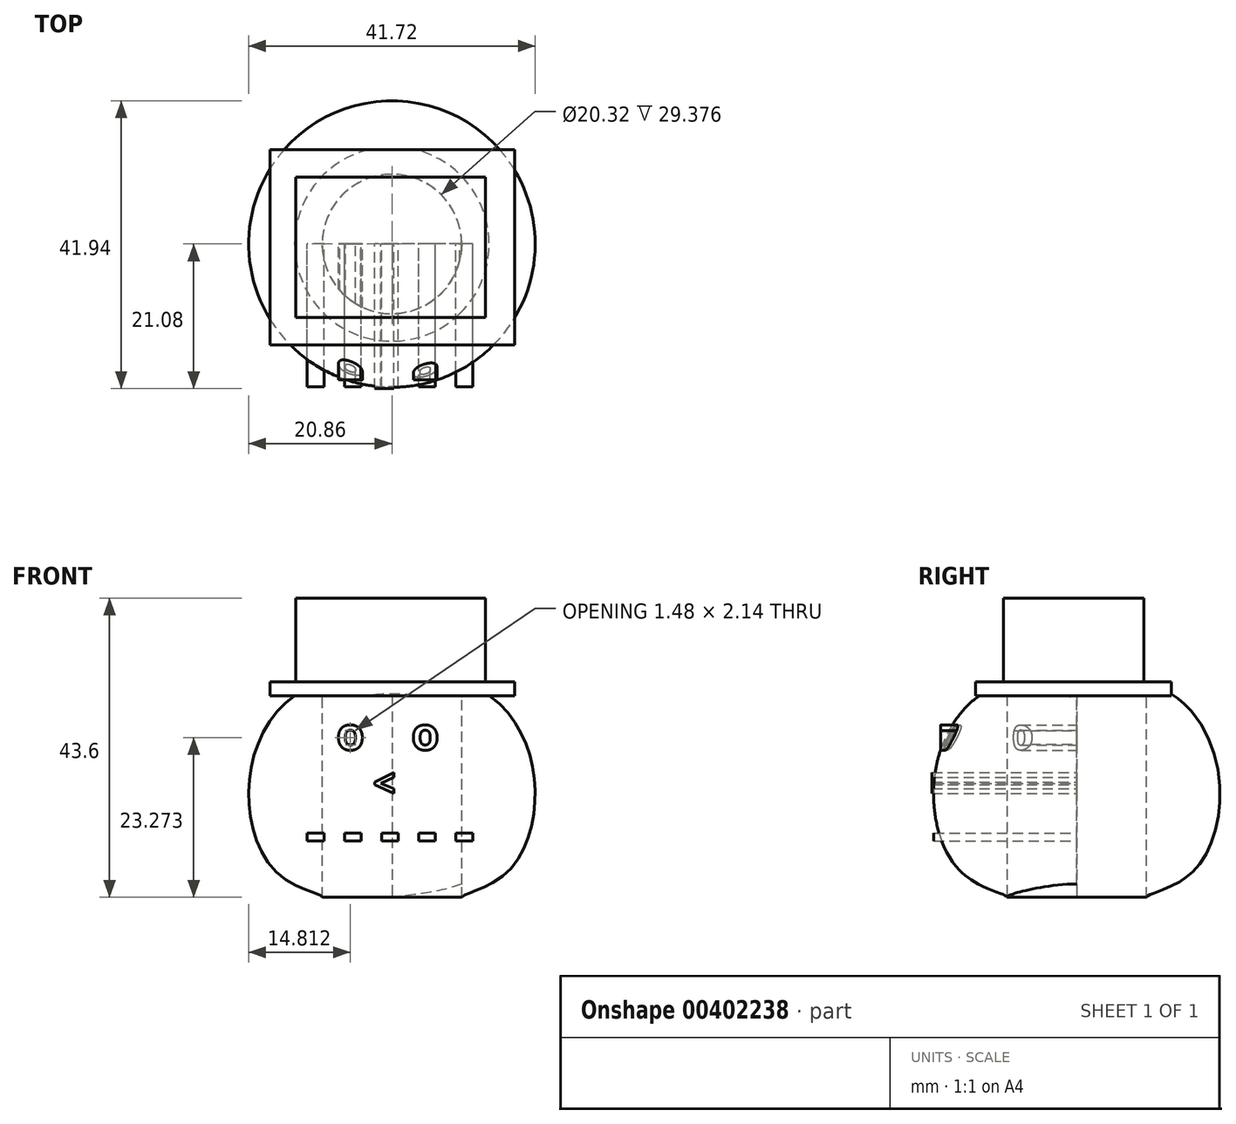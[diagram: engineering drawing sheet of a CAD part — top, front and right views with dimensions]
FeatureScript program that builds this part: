
annotation { "Feature Type Name" : "Feature", "Feature Type Description" : "" }
export const myFeature = defineFeature(function(context is Context, id is Id, definition is map)
    precondition{}
    {
        {
            var Q0;
            Q0=qCreatedBy(makeId("Front.planeOp"),FACE);
            var sketch = newSketch(context, id + "F0", { "sketchPlane" : qUnion([Q0])});
            skLineSegment(sketch, "E0", {"start": v(0, 75.67) * mm, "end": v(0, -75.08) * mm});
            skFitSpline(sketch, "E1", {"points": [v(0, 75.67) * mm, v(11.04, 73.3) * mm, v(17.93, 62.86) * mm, v(14.39, 49.07) * mm, v(0, 44.54) * mm], "startDerivative": vector(50.72, -3) * mm, "endDerivative": vector(-62.09, -7) * mm});
            skSolve(sketch);
        }
        {
            var Q0;
            Q0 = qSketchRegion(id + "F0", true);
            extrude(context, id + "F1", {"entities" : qUnion([Q0]), "depth" : 10.16 * mm});
        }
        {
            var Q0;
            Q0=qCreatedBy(makeId("Front.planeOp"),FACE);
            var sketch = newSketch(context, id + "F2", { "sketchPlane" : qUnion([Q0])});
            skLineSegment(sketch, "E2", {"start": v(0, 76.07) * mm, "end": v(0, 0) * mm});
            skSolve(sketch);
        }
        {
            var Q0;
            Q0=makeQuery(id+"F1.opExtrude","CAP_FACE",FACE,{"disambiguationData":[OSD([sQuery(id+"F0.wireOp",EDGE,"E0"),sQuery(id+"F0.wireOp",EDGE,"E1")])],"isStart":false});
            var Q1;
            Q1=sQuery(id+"F2.wireOp",EDGE,"E2");
            revolve(context, id + "F3", {"operationType" : NewBodyOperationType.ADD, "entities" : qUnion([Q0]), "axis" : qUnion([Q1]), "revolveType" : RevolveType.FULL});
        }
        {
            var Q0;
            Q0=qCreatedBy(makeId("Front.planeOp"),FACE);
            var sketch = newSketch(context, id + "F4", { "sketchPlane" : qUnion([Q0])});
            skText(sketch, "E3", { "text": "o    o", "fontName": "OpenSans-Bold.ttf"});
            const initialGuessF4  = {"E3": [-0.00808, 0.06602, 1, 0, 0.00473]};
            skSetInitialGuess(sketch, initialGuessF4);
            skSolve(sketch);
        }
        {
            var Q0;
            Q0 = qSketchRegion(id + "F4", true);
            extrude(context, id + "F5", {"entities" : qUnion([Q0]), "operationType" : NewBodyOperationType.ADD, "depth" : 19.8 * mm});
        }
        {
            var Q0;
            Q0=qCreatedBy(makeId("Front.planeOp"),FACE);
            var sketch = newSketch(context, id + "F6", { "sketchPlane" : qUnion([Q0])});
            skText(sketch, "E4", { "text": "- - - - -", "fontName": "OpenSans-Bold.ttf"});
            const initialGuessF6  = {"E4": [-0.01261, 0.05084, 1, 0, 0.0067]};
            skSetInitialGuess(sketch, initialGuessF6);
            skSolve(sketch);
        }
        {
            var Q0;
            Q0 = qSketchRegion(id + "F6", true);
            extrude(context, id + "F7", {"entities" : qUnion([Q0]), "depth" : 20.83 * mm});
        }
        {
            var Q0;
            Q0=qCreatedBy(makeId("Top.planeOp"),FACE);
            var sketch = newSketch(context, id + "F8", { "sketchPlane" : qUnion([Q0])});
            skCircle(sketch, "E5", {"center": v(0, 0) * mm, "radius": 25.6 * mm});
            skLineSegment(sketch, "E6.bottom", {"start": v(-42.76, 32.12) * mm, "end": v(43.95, 32.12) * mm});
            skLineSegment(sketch, "E6.top", {"start": v(-42.76, -39.41) * mm, "end": v(43.95, -39.41) * mm});
            skLineSegment(sketch, "E6.left", {"start": v(-42.76, 32.12) * mm, "end": v(-42.76, -39.41) * mm});
            skLineSegment(sketch, "E6.right", {"start": v(43.95, 32.12) * mm, "end": v(43.95, -39.41) * mm});
            skSolve(sketch);
        }
        {
            var Q0;
            Q0=makeQuery(id+"F8.imprint","IMPRINT",FACE,{"disambiguationData":[TD([[makeQuery(id+"F8.imprint","IMPRINT",EDGE,{"derivedFrom":sQuery(id+"F8.wireOp",EDGE,"E5")}),-1.0]])]});
            extrude(context, id + "F9", {"entities" : qUnion([Q0]), "operationType" : NewBodyOperationType.REMOVE, "depth" : 84.58 * mm});
        }
        {
            var Q0;
            Q0=qCreatedBy(makeId("Front.planeOp"),FACE);
            var sketch = newSketch(context, id + "F10", { "sketchPlane" : qUnion([Q0])});
            skText(sketch, "E7", { "text": "<", "fontName": "OpenSans-Bold.ttf"});
            const initialGuessF10  = {"E7": [-0.00276, 0.05912, 1, 0, 0.00414]};
            skSetInitialGuess(sketch, initialGuessF10);
            skSolve(sketch);
        }
        {
            var Q0;
            Q0 = qSketchRegion(id + "F10", true);
            extrude(context, id + "F11", {"entities" : qUnion([Q0]), "depth" : 21.08 * mm});
        }
        {
            var Q0;
            Q0=qCreatedBy(makeId("Top.planeOp"),FACE);
            cPlane(context, id + "F12", {"entities" : qUnion([Q0]), "cplaneType" : CPlaneType.OFFSET, "offset" : 73.9 * mm, "width" : 152.4 * mm, "height" : 152.4 * mm});
        }
        {
            var Q0;
            Q0=qCreatedBy(id+"F12.planeOp",FACE);
            var sketch = newSketch(context, id + "F13", { "sketchPlane" : qUnion([Q0])});
            skLineSegment(sketch, "E8.bottom", {"start": v(-17.75, 13.74) * mm, "end": v(17.9, 13.74) * mm});
            skLineSegment(sketch, "E8.top", {"start": v(-17.75, -14.73) * mm, "end": v(17.9, -14.73) * mm});
            skLineSegment(sketch, "E8.left", {"start": v(-17.75, 13.74) * mm, "end": v(-17.75, -14.73) * mm});
            skLineSegment(sketch, "E8.right", {"start": v(17.9, 13.74) * mm, "end": v(17.9, -14.73) * mm});
            skSolve(sketch);
        }
        {
            var Q0;
            Q0=makeQuery(id+"F13.imprint","IMPRINT",FACE,{"disambiguationData":[TD([[makeQuery(id+"F13.imprint","IMPRINT",EDGE,{"derivedFrom":sQuery(id+"F13.wireOp",EDGE,"E8.bottom")}),-1.0]])]});
            extrude(context, id + "F14", {"entities" : qUnion([Q0]), "operationType" : NewBodyOperationType.ADD, "depth" : 2.03 * mm});
        }
        {
            var Q0;
            Q0=qCreatedBy(id+"F12.planeOp",FACE);
            var sketch = newSketch(context, id + "F15", { "sketchPlane" : qUnion([Q0])});
            skLineSegment(sketch, "E9.bottom", {"start": v(-14.01, 9.77) * mm, "end": v(13.64, 9.77) * mm});
            skLineSegment(sketch, "E9.top", {"start": v(-14.01, -10.7) * mm, "end": v(13.64, -10.7) * mm});
            skLineSegment(sketch, "E9.left", {"start": v(-14.01, 9.77) * mm, "end": v(-14.01, -10.7) * mm});
            skLineSegment(sketch, "E9.right", {"start": v(13.64, 9.77) * mm, "end": v(13.64, -10.7) * mm});
            skSolve(sketch);
        }
        {
            var Q0;
            Q0 = qSketchRegion(id + "F15", true);
            extrude(context, id + "F16", {"entities" : qUnion([Q0]), "operationType" : NewBodyOperationType.ADD, "depth" : 14.22 * mm});
        }
    });
